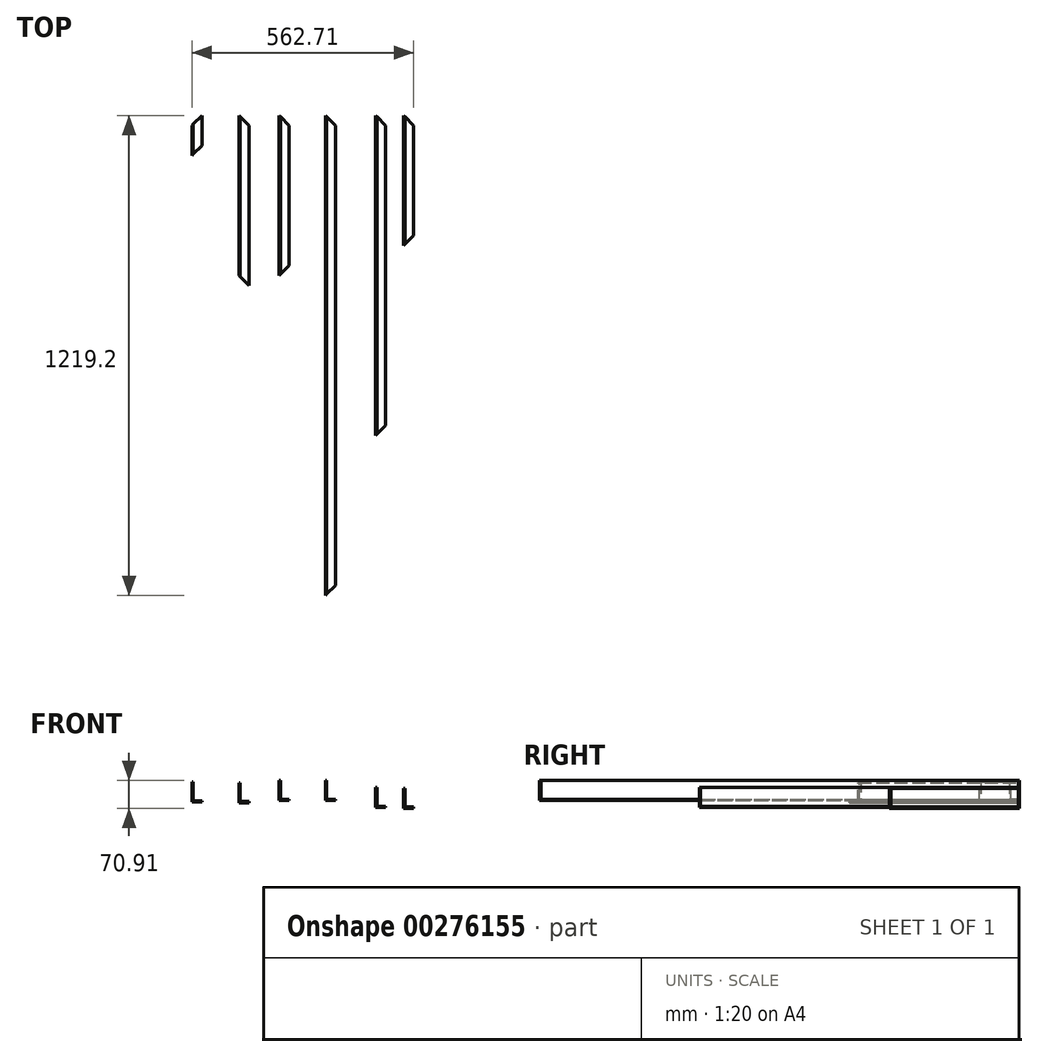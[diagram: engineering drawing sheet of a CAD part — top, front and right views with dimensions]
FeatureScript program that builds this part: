
annotation { "Feature Type Name" : "Feature", "Feature Type Description" : "" }
export const myFeature = defineFeature(function(context is Context, id is Id, definition is map)
    precondition{}
    {
        {
            var Q0;
            Q0=qCreatedBy(makeId("Front.planeOp"),FACE);
            var sketch = newSketch(context, id + "F0", { "sketchPlane" : qUnion([Q0])});
            skLineSegment(sketch, "E0", {"start": v(0, 0) * mm, "end": v(0, 50.8) * mm});
            skLineSegment(sketch, "E1", {"start": v(0, 0) * mm, "end": v(25.4, 0) * mm});
            skLineSegment(sketch, "E2", {"start": v(25.4, 0) * mm, "end": v(25.4, 3.18) * mm});
            skLineSegment(sketch, "E3", {"start": v(25.4, 3.18) * mm, "end": v(3.18, 3.17) * mm});
            skLineSegment(sketch, "E4", {"start": v(3.18, 3.17) * mm, "end": v(3.18, 50.8) * mm});
            skLineSegment(sketch, "E5", {"start": v(3.18, 50.8) * mm, "end": v(0, 50.8) * mm});
            skSolve(sketch);
        }
        {
            var Q0;
            Q0 = qSketchRegion(id + "F0", true);
            extrude(context, id + "F1", {"entities" : qUnion([Q0]), "depth" : 1219.2 * mm});
        }
        {
            var Q0;
            Q0=qCreatedBy(makeId("Front.planeOp"),FACE);
            var sketch = newSketch(context, id + "F2", { "sketchPlane" : qUnion([Q0])});
            skLineSegment(sketch, "E6", {"start": v(-117.04, 0) * mm, "end": v(-117.04, 50.8) * mm});
            skLineSegment(sketch, "E7", {"start": v(-117.04, 0) * mm, "end": v(-91.64, 0) * mm});
            skLineSegment(sketch, "E8", {"start": v(-91.64, 0) * mm, "end": v(-91.64, 3.17) * mm});
            skLineSegment(sketch, "E9", {"start": v(-91.64, 3.17) * mm, "end": v(-113.86, 3.17) * mm});
            skLineSegment(sketch, "E10", {"start": v(-113.86, 3.17) * mm, "end": v(-113.86, 50.8) * mm});
            skLineSegment(sketch, "E11", {"start": v(-113.86, 50.8) * mm, "end": v(-117.04, 50.8) * mm});
            skSolve(sketch);
        }
        {
            var Q0;
            Q0 = qSketchRegion(id + "F2", true);
            extrude(context, id + "F3", {"entities" : qUnion([Q0]), "depth" : 406.4 * mm});
        }
        {
            var Q0;
            Q0=makeQuery(id+"F3.opExtrude","CAP_EDGE",EDGE,{"disambiguationData":[OSD([sQuery(id+"F2.wireOp",EDGE,"E8")])],"isStart":false});
            var Q1;
            Q1=makeQuery(id+"F1.opExtrude","CAP_EDGE",EDGE,{"disambiguationData":[OSD([sQuery(id+"F0.wireOp",EDGE,"E2")])],"isStart":false});
            var Q2;
            Q2=makeQuery(id+"F1.opExtrude","CAP_EDGE",EDGE,{"disambiguationData":[OSD([sQuery(id+"F0.wireOp",EDGE,"E2")])],"isStart":true});
            var Q3;
            Q3=makeQuery(id+"F3.opExtrude","CAP_EDGE",EDGE,{"disambiguationData":[OSD([sQuery(id+"F2.wireOp",EDGE,"E8")])],"isStart":true});
            chamfer(context, id + "F4", {"entities" : qUnion([Q0, Q1, Q2, Q3]), "width" : 25.4 * mm, "tangentPropagation" : true});
        }
        {
            var Q0;
            Q0=qCreatedBy(makeId("Front.planeOp"),FACE);
            var sketch = newSketch(context, id + "F5", { "sketchPlane" : qUnion([Q0])});
            skLineSegment(sketch, "E12", {"start": v(128.13, -18) * mm, "end": v(128.13, 32.8) * mm});
            skLineSegment(sketch, "E13", {"start": v(128.13, -18) * mm, "end": v(153.53, -18) * mm});
            skLineSegment(sketch, "E14", {"start": v(153.53, -18) * mm, "end": v(153.53, -14.82) * mm});
            skLineSegment(sketch, "E15", {"start": v(153.53, -14.82) * mm, "end": v(131.3, -14.82) * mm});
            skLineSegment(sketch, "E16", {"start": v(131.3, -14.82) * mm, "end": v(131.3, 32.8) * mm});
            skLineSegment(sketch, "E17", {"start": v(131.3, 32.8) * mm, "end": v(128.13, 32.8) * mm});
            skSolve(sketch);
        }
        {
            var Q0;
            Q0 = qSketchRegion(id + "F5", true);
            extrude(context, id + "F6", {"entities" : qUnion([Q0]), "depth" : 812.8 * mm});
        }
        {
            var Q0;
            Q0=qCreatedBy(makeId("Front.planeOp"),FACE);
            var sketch = newSketch(context, id + "F7", { "sketchPlane" : qUnion([Q0])});
            skLineSegment(sketch, "E18", {"start": v(198.68, -20.11) * mm, "end": v(198.68, 30.69) * mm});
            skLineSegment(sketch, "E19", {"start": v(198.68, -20.11) * mm, "end": v(224.08, -20.11) * mm});
            skLineSegment(sketch, "E20", {"start": v(224.08, -20.11) * mm, "end": v(224.08, -16.94) * mm});
            skLineSegment(sketch, "E21", {"start": v(224.08, -16.94) * mm, "end": v(201.85, -16.94) * mm});
            skLineSegment(sketch, "E22", {"start": v(201.85, -16.94) * mm, "end": v(201.85, 30.69) * mm});
            skLineSegment(sketch, "E23", {"start": v(201.85, 30.69) * mm, "end": v(198.68, 30.69) * mm});
            skSolve(sketch);
        }
        {
            var Q0;
            Q0=makeQuery(id+"F7.imprint","IMPRINT",FACE,{"disambiguationData":[TD([[makeQuery(id+"F7.imprint","IMPRINT",EDGE,{"derivedFrom":sQuery(id+"F7.wireOp",EDGE,"E18")}),-1.0]])]});
            extrude(context, id + "F8", {"entities" : qUnion([Q0]), "depth" : 330.2 * mm});
        }
        {
            var Q0;
            Q0=makeQuery(id+"F6.opExtrude","CAP_EDGE",EDGE,{"disambiguationData":[OSD([sQuery(id+"F5.wireOp",EDGE,"E14")])],"isStart":true});
            var Q1;
            Q1=makeQuery(id+"F8.opExtrude","CAP_EDGE",EDGE,{"disambiguationData":[OSD([sQuery(id+"F7.wireOp",EDGE,"E20")])],"isStart":true});
            var Q2;
            Q2=makeQuery(id+"F6.opExtrude","CAP_EDGE",EDGE,{"disambiguationData":[OSD([sQuery(id+"F5.wireOp",EDGE,"E14")])],"isStart":false});
            var Q3;
            Q3=makeQuery(id+"F8.opExtrude","CAP_EDGE",EDGE,{"disambiguationData":[OSD([sQuery(id+"F7.wireOp",EDGE,"E20")])],"isStart":false});
            chamfer(context, id + "F9", {"entities" : qUnion([Q0, Q1, Q2, Q3]), "width" : 25.4 * mm, "tangentPropagation" : true});
        }
        {
            var Q0;
            Q0=qCreatedBy(makeId("Front.planeOp"),FACE);
            var sketch = newSketch(context, id + "F10", { "sketchPlane" : qUnion([Q0])});
            skLineSegment(sketch, "E24", {"start": v(-219.2, -6.03) * mm, "end": v(-219.2, 44.77) * mm});
            skLineSegment(sketch, "E25", {"start": v(-219.2, -6.03) * mm, "end": v(-193.8, -6.03) * mm});
            skLineSegment(sketch, "E26", {"start": v(-193.8, -6.03) * mm, "end": v(-193.8, -2.86) * mm});
            skLineSegment(sketch, "E27", {"start": v(-193.8, -2.86) * mm, "end": v(-216.03, -2.86) * mm});
            skLineSegment(sketch, "E28", {"start": v(-216.03, -2.86) * mm, "end": v(-216.03, 44.77) * mm});
            skLineSegment(sketch, "E29", {"start": v(-216.03, 44.77) * mm, "end": v(-219.2, 44.77) * mm});
            skSolve(sketch);
        }
        {
            var Q0;
            Q0 = qSketchRegion(id + "F10", true);
            extrude(context, id + "F11", {"entities" : qUnion([Q0]), "depth" : 431.8 * mm});
        }
        {
            var Q0;
            Q0=qCreatedBy(makeId("Front.planeOp"),FACE);
            var sketch = newSketch(context, id + "F12", { "sketchPlane" : qUnion([Q0])});
            skLineSegment(sketch, "E30", {"start": v(-338.63, -4.06) * mm, "end": v(-338.63, 46.74) * mm});
            skLineSegment(sketch, "E31", {"start": v(-338.63, -4.06) * mm, "end": v(-313.23, -4.06) * mm});
            skLineSegment(sketch, "E32", {"start": v(-313.23, -4.06) * mm, "end": v(-313.23, -0.88) * mm});
            skLineSegment(sketch, "E33", {"start": v(-313.23, -0.88) * mm, "end": v(-335.45, -0.88) * mm});
            skLineSegment(sketch, "E34", {"start": v(-335.45, -0.88) * mm, "end": v(-335.45, 46.74) * mm});
            skLineSegment(sketch, "E35", {"start": v(-335.45, 46.74) * mm, "end": v(-338.63, 46.74) * mm});
            skSolve(sketch);
        }
        {
            var Q0;
            Q0 = qSketchRegion(id + "F12", true);
            extrude(context, id + "F13", {"entities" : qUnion([Q0]), "depth" : 101.6 * mm});
        }
        {
            var Q0;
            Q0=makeQuery(id+"F11.opExtrude","CAP_EDGE",EDGE,{"disambiguationData":[OSD([sQuery(id+"F10.wireOp",EDGE,"E24")])],"isStart":false});
            chamfer(context, id + "F14", {"entities" : qUnion([Q0]), "width" : 25.4 * mm, "tangentPropagation" : true});
        }
        {
            var Q0;
            Q0=makeQuery(id+"F11.opExtrude","CAP_EDGE",EDGE,{"disambiguationData":[OSD([sQuery(id+"F10.wireOp",EDGE,"E26")])],"isStart":true});
            chamfer(context, id + "F15", {"entities" : qUnion([Q0]), "width" : 25.4 * mm, "tangentPropagation" : true});
        }
        {
            var Q0;
            Q0=makeQuery(id+"F13.opExtrude","CAP_EDGE",EDGE,{"disambiguationData":[OSD([sQuery(id+"F12.wireOp",EDGE,"E32")])],"isStart":false});
            chamfer(context, id + "F16", {"entities" : qUnion([Q0]), "width" : 25.4 * mm, "tangentPropagation" : true});
        }
        {
            var Q0;
            Q0=makeQuery(id+"F13.opExtrude","CAP_EDGE",EDGE,{"disambiguationData":[OSD([sQuery(id+"F12.wireOp",EDGE,"E30")])],"isStart":true});
            chamfer(context, id + "F17", {"entities" : qUnion([Q0]), "width" : 25.4 * mm, "tangentPropagation" : true});
        }
    });
